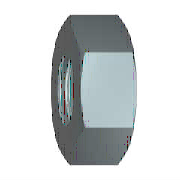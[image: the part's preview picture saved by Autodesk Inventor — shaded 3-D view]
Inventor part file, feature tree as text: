
AUTODESK INVENTOR PART (.ipt)
format: ipt  version: 2024.3 (Build 283343000, 343)  size: 160,768 bytes
history: native  units: mm (DEFAULTED — no unit token found)
features: chamfer x1, hole x1, other x1, plane x1
ambient origin geometry x7: Origin, YZ Plane, XZ Plane, X Axis, Y Axis, Z Axis, Center Point
bodies: Solid1 (feature_tree), Body (feature_tree)
feature tree (4):
  chamfer  "Chamfer1"  Distance=9.237604mm
  hole  "Thread"  [1 undecoded]
  other  "Work Axis1"
  plane  "Work Plane1"
note: 1 required parameter value undecoded (feature->parameter linkage not recoverable at this tier; creation-order binding heuristic only, values carry confidence <= 0.55)
